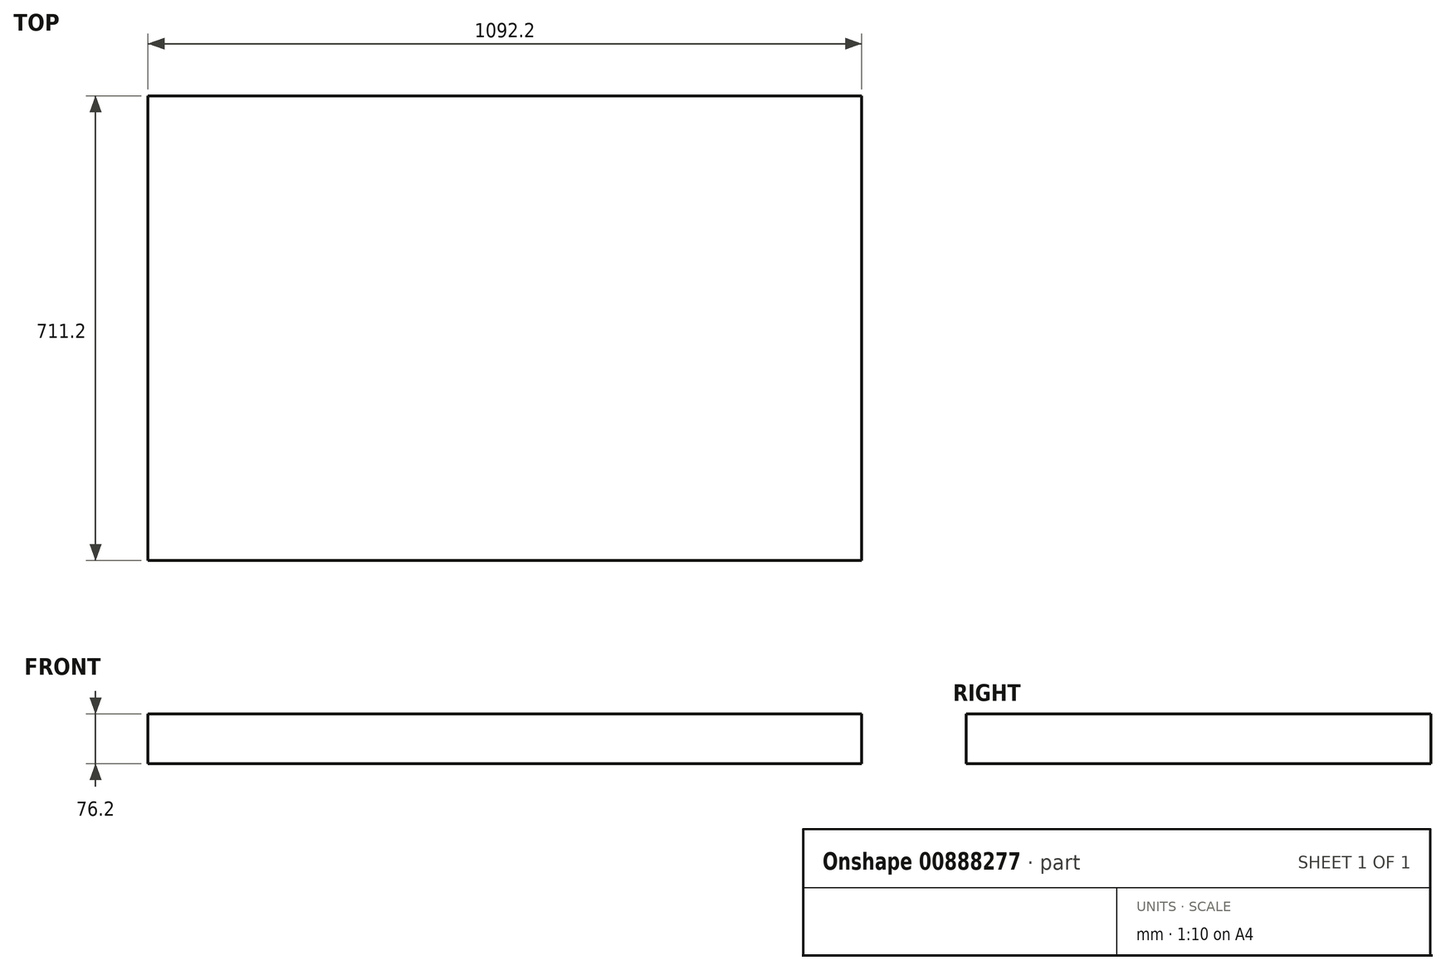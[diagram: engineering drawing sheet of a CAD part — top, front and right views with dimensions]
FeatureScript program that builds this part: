
annotation { "Feature Type Name" : "Feature", "Feature Type Description" : "" }
export const myFeature = defineFeature(function(context is Context, id is Id, definition is map)
    precondition{}
    {
        {
            var Q0;
            Q0=qCreatedBy(makeId("Top.planeOp"),FACE);
            var sketch = newSketch(context, id + "F0", { "sketchPlane" : qUnion([Q0])});
            skLineSegment(sketch, "E0.bottom", {"start": v(0, 0) * mm, "end": v(1092.2, 0) * mm});
            skLineSegment(sketch, "E0.top", {"start": v(0, -711.2) * mm, "end": v(1092.2, -711.2) * mm});
            skLineSegment(sketch, "E0.left", {"start": v(0, 0) * mm, "end": v(0, -711.2) * mm});
            skLineSegment(sketch, "E0.right", {"start": v(1092.2, 0) * mm, "end": v(1092.2, -711.2) * mm});
            skSolve(sketch);
        }
        {
            var Q0;
            Q0=makeQuery(id+"F0.imprint","IMPRINT",FACE,{"disambiguationData":[TD([[makeQuery(id+"F0.imprint","IMPRINT",EDGE,{"derivedFrom":sQuery(id+"F0.wireOp",EDGE,"E0.bottom")}),-1.0]])]});
            extrude(context, id + "F1", {"entities" : qUnion([Q0]), "depth" : 76.2 * mm, "offsetDistance" : 25.4 * mm});
        }
    });
